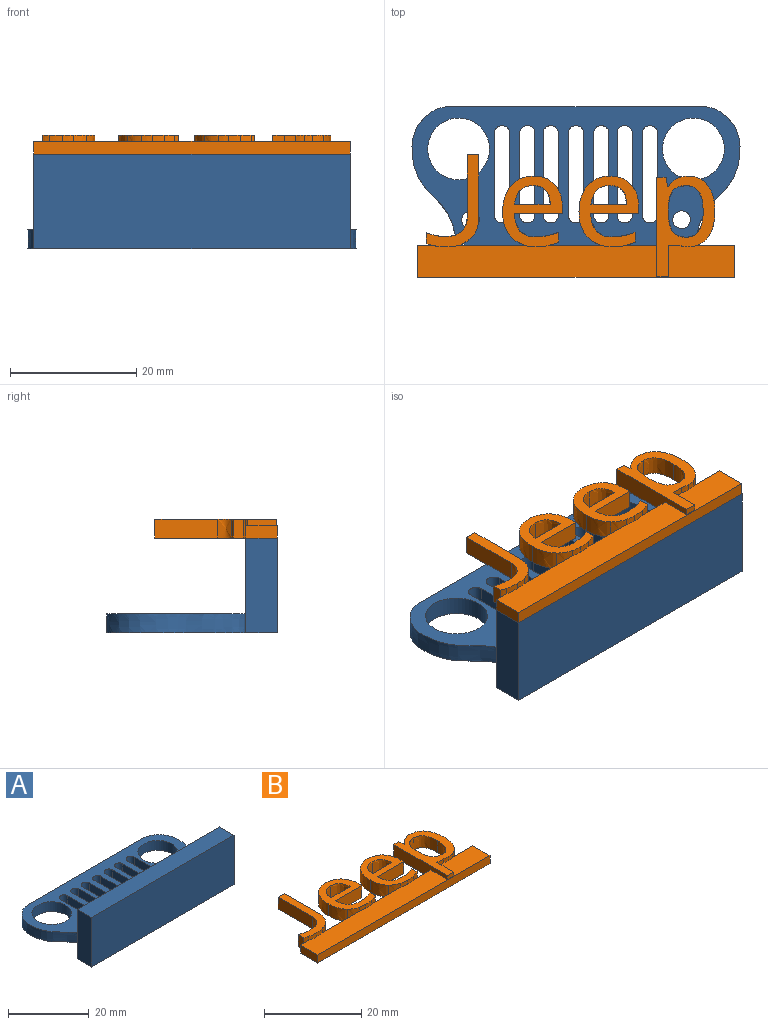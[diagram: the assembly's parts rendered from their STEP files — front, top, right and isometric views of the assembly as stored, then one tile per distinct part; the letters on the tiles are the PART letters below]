
ASSEMBLY  parts=2 mates=1
PART A: 42 faces, bbox 51.9x27x15 mm
  f0: plane 40.9x3mm, normal (0,1,0), area 122.7mm2, adj f1,f34,f35,f36
  f1: extruded ~22.01x8.86mm, area 87.7mm2, adj f0,f35,f36,f38
  f2: plane 13x3mm, normal (1,0,0), area 39mm2, adj f3,f23,f35,f36
  f3: cylinder r=1.2mm len=3mm, axis (0,0,-1), area 11.3mm2, adj f2,f4,f35,f36
  f4: plane 13x3mm, normal (-1,0,0), area 39mm2, adj f3,f23,f35,f36
  f5: plane 13x3mm, normal (1,0,0), area 39mm2, adj f6,f24,f35,f36
  f6: cylinder r=1.2mm len=3mm, axis (0,0,-1), area 11.3mm2, adj f5,f7,f35,f36
  f7: plane 13x3mm, normal (-1,0,0), area 39mm2, adj f6,f24,f35,f36
  f8: plane 13x3mm, normal (1,0,0), area 39mm2, adj f9,f25,f35,f36
  f9: cylinder r=1.2mm len=3mm, axis (0,0,-1), area 11.3mm2, adj f8,f10,f35,f36
  f10: plane 13x3mm, normal (-1,0,0), area 39mm2, adj f9,f25,f35,f36
  f11: plane 13x3mm, normal (1,0,0), area 39mm2, adj f12,f26,f35,f36
  f12: cylinder r=1.2mm len=3mm, axis (0,0,-1), area 11.3mm2, adj f11,f13,f35,f36
  f13: plane 13x3mm, normal (-1,0,0), area 39mm2, adj f12,f26,f35,f36
  f14: plane 13x3mm, normal (1,0,0), area 39mm2, adj f15,f27,f35,f36
  f15: cylinder r=1.2mm len=3mm, axis (0,0,-1), area 11.3mm2, adj f14,f16,f35,f36
  f16: plane 13x3mm, normal (-1,0,0), area 39mm2, adj f15,f27,f35,f36
  f17: plane 13x3mm, normal (1,0,0), area 39mm2, adj f18,f28,f35,f36
  f18: cylinder r=1.2mm len=3mm, axis (0,0,-1), area 11.3mm2, adj f17,f19,f35,f36
  f19: plane 13x3mm, normal (-1,0,0), area 39mm2, adj f18,f28,f35,f36
  f20: plane 13x3mm, normal (-1,0,0), area 39mm2, adj f21,f33,f35,f36
  f21: cylinder r=1.2mm len=3mm, axis (0,0,-1), area 11.3mm2, adj f20,f22,f35,f36
  f22: plane 13x3mm, normal (1,0,0), area 39mm2, adj f21,f33,f35,f36
  f23: cylinder r=1.2mm len=3mm, axis (0,0,-1), area 11.3mm2, adj f2,f4,f35,f36
  f24: cylinder r=1.2mm len=3mm, axis (0,0,-1), area 11.3mm2, adj f5,f7,f35,f36
  f25: cylinder r=1.2mm len=3mm, axis (0,0,-1), area 11.3mm2, adj f8,f10,f35,f36
  f26: cylinder r=1.2mm len=3mm, axis (0,0,-1), area 11.3mm2, adj f11,f13,f35,f36
  f27: cylinder r=1.2mm len=3mm, axis (0,0,-1), area 11.3mm2, adj f14,f16,f35,f36
  f28: cylinder r=1.2mm len=3mm, axis (0,0,-1), area 11.3mm2, adj f17,f19,f35,f36
  f29: cylinder r=1.4mm len=3mm, axis (0,0,-1), area 26.4mm2, adj f35,f36
  f30: cylinder r=4.89mm len=9.78mm, axis (0,0,-1), area 92.2mm2, adj f35,f36
  f31: cylinder r=4.89mm len=9.78mm, axis (0,0,-1), area 92.2mm2, adj f35,f36
  f32: cylinder r=1.4mm len=3mm, axis (0,0,-1), area 26.4mm2, adj f35,f36
  f33: cylinder r=1.2mm len=3mm, axis (0,0,-1), area 11.3mm2, adj f20,f22,f35,f36
  f34: extruded ~22.01x8.86mm, area 87.7mm2, adj f0,f35,f36,f38
  f35: plane 51.91x22.01mm, normal (0,0,1), area 607.3mm2, adj f0,f1,f2,f3,f4,f5,f6,f7
  f36: plane 51.91x27.01mm, normal (0,0,-1), area 857.3mm2, adj f0,f1,f2,f3,f4,f5,f6,f7
  f37: plane 15x5mm, normal (1,0,0), area 75mm2, adj f36,f38,f40,f41
  f38: plane 50x15mm, normal (0,1,0), area 647.5mm2, adj f1,f34,f35,f36,f37,f39,f41
  f39: plane 15x5mm, normal (-1,0,0), area 75mm2, adj f36,f38,f40,f41
  f40: plane 50x15mm, normal (0,-1,0), area 750mm2, adj f36,f37,f39,f41
  f41: plane 50x5mm, normal (0,0,1), area 250mm2, adj f37,f38,f39,f40
PART B: 82 faces, bbox 50x19.4x3 mm
  f0: plane 5.92x2mm, normal (0,1,0), area 11.8mm2, adj f7,f8,f9,f69
  f1: plane 5.1x2mm, normal (0,1,0), area 10.2mm2, adj f8,f9,f44,f77
  f2: plane 8.51x2mm, normal (0,1,0), area 17mm2, adj f8,f9,f26,f55
  f3: plane 2.41x2mm, normal (0,1,0), area 4.8mm2, adj f5,f8,f9,f12
  f4: plane 10.81x2mm, normal (0,1,0), area 21.6mm2, adj f8,f9,f15,f37
  f5: plane 5x2mm, normal (-1,0,0), area 10mm2, adj f3,f6,f8,f9
  f6: plane 50x2mm, normal (0,-1,0), area 100mm2, adj f5,f7,f8,f9
  f7: plane 5x2mm, normal (1,0,0), area 10mm2, adj f0,f6,f8,f9
  f8: plane 50x5mm, normal (0,0,1), area 239.5mm2, adj f0,f1,f2,f3,f4,f5,f6,f7
  f9: plane 50x19.37mm, normal (0,0,-1), area 436.4mm2, adj f0,f1,f2,f3,f4,f5,f6,f7
  f10: extruded ~3.04x3mm, area 9.3mm2, adj f9,f11,f21,f22
  f11: plane 3x1.63mm, normal (-1,0,0), area 4.9mm2, adj f9,f10,f12,f22
  f12: extruded ~3x1.06mm, area 3.4mm2, adj f3,f9,f11,f13,f22
  f13: extruded ~2.12x1mm, area 2.1mm2, adj f8,f12,f14,f22
  f14: extruded ~1.7x1mm, area 1.7mm2, adj f8,f13,f15,f22
  f15: extruded ~3x2.01mm, area 6.9mm2, adj f4,f9,f14,f16,f22
  f16: extruded ~3.38x3mm, area 11.3mm2, adj f9,f15,f17,f22
  f17: plane 9.94x3mm, normal (1,0,0), area 29.8mm2, adj f9,f16,f18,f22
  f18: plane 3x1.83mm, normal (0,1,0), area 5.5mm2, adj f9,f17,f19,f22
  f19: plane 9.96x3mm, normal (-1,0,0), area 29.9mm2, adj f9,f18,f20,f22
  f20: extruded ~3x2.23mm, area 7.5mm2, adj f9,f19,f21,f22
  f21: extruded ~3x2.5mm, area 8mm2, adj f9,f10,f20,f22
  f22: plane 14.57x8.28mm, normal (0,0,1), area 34.5mm2, adj f10,f11,f12,f13,f14,f15,f16,f17
  f23: plane 5.63x3mm, normal (0,1,0), area 16.9mm2, adj f9,f24,f39,f40
  f24: extruded ~3x3mm, area 14.2mm2, adj f9,f23,f39,f40
  f25: extruded ~1.93x1mm, area 1.9mm2, adj f8,f26,f38,f40
  f26: extruded ~3x1.65mm, area 5.2mm2, adj f2,f9,f25,f27,f40
  f27: plane 3x1.57mm, normal (1,0,0), area 4.7mm2, adj f9,f26,f28,f40
  f28: extruded ~3.64x3mm, area 11.2mm2, adj f9,f27,f29,f40
  f29: extruded ~3.69x3.38mm, area 17.1mm2, adj f9,f28,f30,f40
  f30: plane 7.61x3mm, normal (0,-1,0), area 22.8mm2, adj f9,f29,f31,f40
  f31: plane 3x1.11mm, normal (1,0,0), area 3.3mm2, adj f9,f30,f32,f40
  f32: extruded ~3.51x3mm, area 11.5mm2, adj f9,f31,f33,f40
  f33: extruded ~3.33x3mm, area 11.1mm2, adj f9,f32,f34,f40
  f34: extruded ~3.56x3mm, area 12mm2, adj f9,f33,f35,f40
  f35: extruded ~4.14x3mm, area 13.3mm2, adj f9,f34,f36,f40
  f36: extruded ~4.05x3mm, area 13.2mm2, adj f9,f35,f37,f40
  f37: extruded ~3x2.21mm, area 7.8mm2, adj f4,f9,f36,f38,f40
  f38: extruded ~1.64x1mm, area 1.7mm2, adj f8,f25,f37,f40
  f39: extruded ~3x3mm, area 13.8mm2, adj f9,f23,f24,f40
  f40: plane 11.19x9.46mm, normal (0,0,1), area 50.5mm2, adj f23,f24,f25,f26,f27,f28,f29,f30
  f41: plane 5.63x3mm, normal (0,1,0), area 16.9mm2, adj f9,f42,f57,f58
  f42: extruded ~3x3mm, area 14.2mm2, adj f9,f41,f57,f58
  f43: extruded ~1.93x1mm, area 1.9mm2, adj f8,f44,f56,f58
  f44: extruded ~3x1.65mm, area 5.2mm2, adj f1,f9,f43,f45,f58
  f45: plane 3x1.57mm, normal (1,0,0), area 4.7mm2, adj f9,f44,f46,f58
  f46: extruded ~3.64x3mm, area 11.2mm2, adj f9,f45,f47,f58
  f47: extruded ~3.69x3.38mm, area 17.1mm2, adj f9,f46,f48,f58
  f48: plane 7.61x3mm, normal (0,-1,0), area 22.8mm2, adj f9,f47,f49,f58
  f49: plane 3x1.11mm, normal (1,0,0), area 3.3mm2, adj f9,f48,f50,f58
  f50: extruded ~3.51x3mm, area 11.5mm2, adj f9,f49,f51,f58
  f51: extruded ~3.33x3mm, area 11.1mm2, adj f9,f50,f52,f58
  f52: extruded ~3.56x3mm, area 12mm2, adj f9,f51,f53,f58
  f53: extruded ~4.14x3mm, area 13.3mm2, adj f9,f52,f54,f58
  f54: extruded ~4.05x3mm, area 13.2mm2, adj f9,f53,f55,f58
  f55: extruded ~3x2.21mm, area 7.8mm2, adj f2,f9,f54,f56,f58
  f56: extruded ~1.64x1mm, area 1.7mm2, adj f8,f43,f55,f58
  f57: extruded ~3x3mm, area 13.8mm2, adj f9,f41,f42,f58
  f58: plane 11.19x9.46mm, normal (0,0,1), area 50.5mm2, adj f41,f42,f43,f44,f45,f46,f47,f48
  f59: plane 1.84x1mm, normal (0,-1,0), area 1.8mm2, adj f8,f66,f67,f81
  f60: plane 3x0.4mm, normal (1,0,0), area 1.2mm2, adj f9,f61,f80,f81
  f61: extruded ~3x2.82mm, area 8.8mm2, adj f9,f60,f62,f81
  f62: extruded ~3x2.15mm, area 7.2mm2, adj f9,f61,f63,f81
  f63: extruded ~4.07x3mm, area 16.6mm2, adj f9,f62,f64,f81
  f64: extruded ~4.15x3mm, area 16.8mm2, adj f9,f63,f65,f81
  f65: extruded ~3x2.18mm, area 7.4mm2, adj f9,f64,f80,f81
  f66: extruded ~1x0.23mm, area 0.2mm2, adj f8,f59,f79,f81
  f67: extruded ~1.33x1mm, area 1.4mm2, adj f8,f59,f68,f81
  f68: extruded ~1.33x1mm, area 1.3mm2, adj f8,f67,f69,f81
  f69: extruded ~3x1.77mm, area 6.7mm2, adj f0,f9,f68,f70,f81
  f70: extruded ~4.13x3mm, area 13.1mm2, adj f9,f69,f71,f81
  f71: extruded ~4.1x3mm, area 13mm2, adj f9,f70,f72,f81
  f72: extruded ~3.1x3mm, area 10.7mm2, adj f9,f71,f73,f81
  f73: extruded ~3.16x3mm, area 11.2mm2, adj f9,f72,f74,f81
  f74: plane 3x0.08mm, normal (0,1,0), area 0.2mm2, adj f9,f73,f75,f81
  f75: plane 3x1.45mm, normal (0.98,0.18,0), area 4.4mm2, adj f9,f74,f76,f81
  f76: plane 3x1.44mm, normal (0,1,0), area 4.3mm2, adj f9,f75,f77,f81
  f77: plane 15.63x3mm, normal (-1,0,0), area 37.2mm2, adj f1,f8,f9,f76,f78,f81
  f78: plane 1.79x1mm, normal (0,-1,0), area 1.8mm2, adj f8,f77,f79,f81
  f79: plane 4.61x1mm, normal (1,0,0), area 4.6mm2, adj f8,f66,f78,f81
  f80: extruded ~3.18x3mm, area 9.9mm2, adj f9,f60,f65,f81
  f81: plane 15.83x9.18mm, normal (0,0,1), area 61.5mm2, adj f59,f60,f61,f62,f63,f64,f65,f66
PLACE A t=(-13.71,3.84,6.38)mm fixed
PLACE B t=(-13.71,26.87,21.38)mm
MATE fastened B.f7 <-> A.f37  axis (1,0,0) through (11.29,-12.16,21.38)mm
